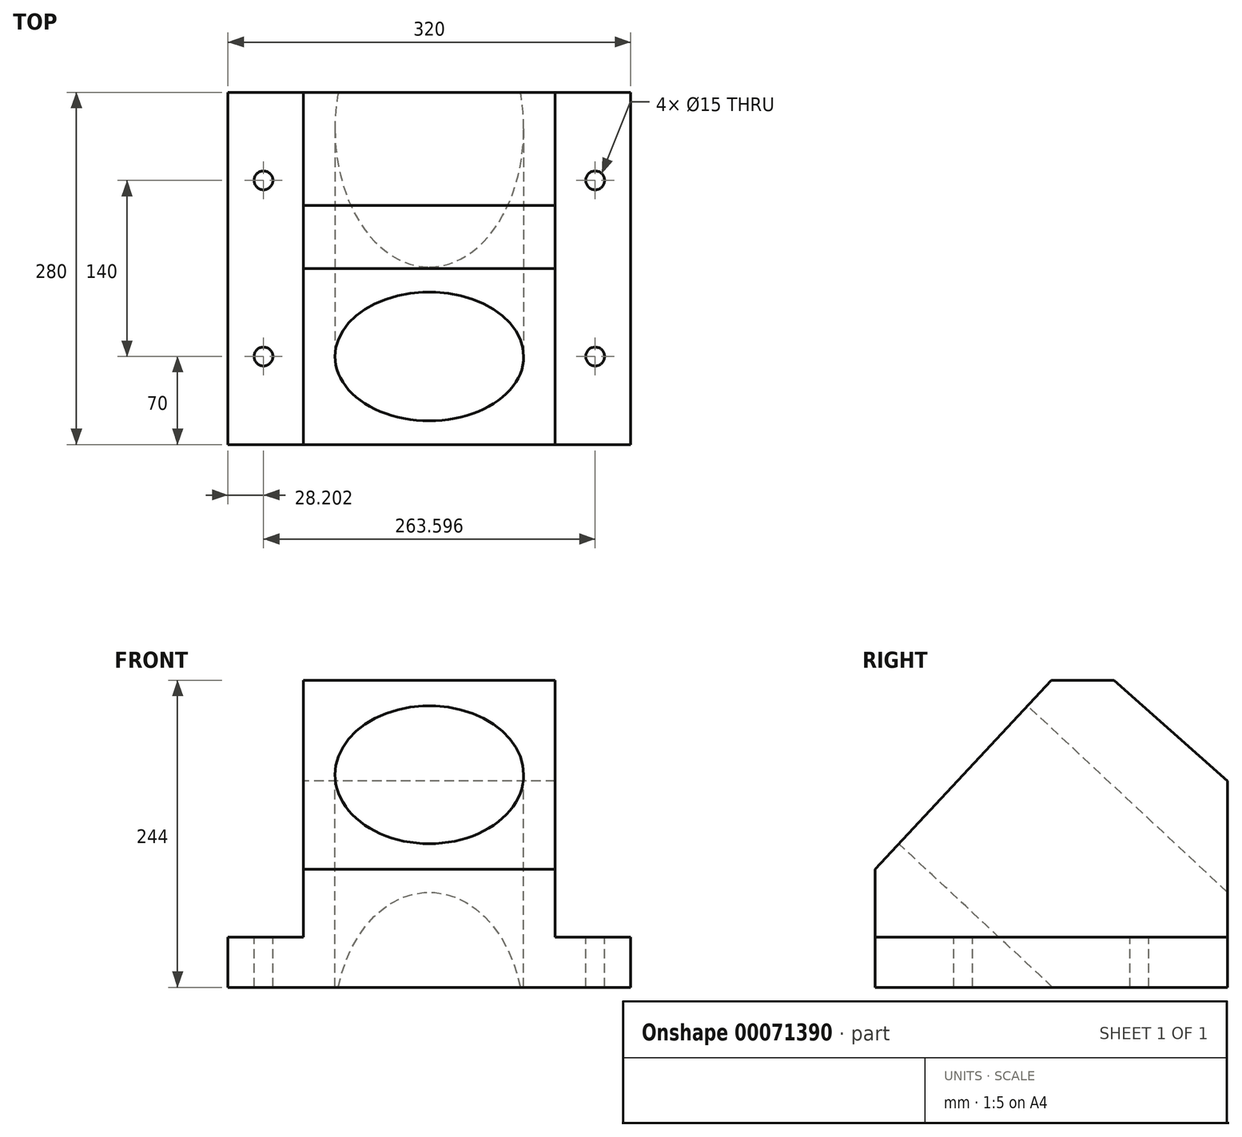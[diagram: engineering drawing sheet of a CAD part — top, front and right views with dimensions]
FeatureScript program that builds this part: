
annotation { "Feature Type Name" : "Feature", "Feature Type Description" : "" }
export const myFeature = defineFeature(function(context is Context, id is Id, definition is map)
    precondition{}
    {
        {
            var Q0;
            Q0=qCreatedBy(makeId("Right.planeOp"),FACE);
            var sketch = newSketch(context, id + "F0", { "sketchPlane" : qUnion([Q0])});
            skLineSegment(sketch, "E0", {"start": v(-140, -32.48) * mm, "end": v(140, -32.48) * mm});
            skLineSegment(sketch, "E1", {"start": v(-140, -32.48) * mm, "end": v(-140, 7.52) * mm});
            skLineSegment(sketch, "E2", {"start": v(-140, 7.52) * mm, "end": v(140, 7.52) * mm});
            skLineSegment(sketch, "E3", {"start": v(140, 7.52) * mm, "end": v(140, -32.48) * mm});
            skLineSegment(sketch, "E4", {"start": v(-140, 7.52) * mm, "end": v(-140, 61.52) * mm});
            skLineSegment(sketch, "E5", {"start": v(140, 7.52) * mm, "end": v(140, 131.52) * mm});
            skLineSegment(sketch, "E6", {"start": v(0, 211.52) * mm, "end": v(50, 211.52) * mm});
            skLineSegment(sketch, "E7", {"start": v(50, 211.52) * mm, "end": v(140, 131.52) * mm});
            skLineSegment(sketch, "E8", {"start": v(0, 211.52) * mm, "end": v(-140, 61.52) * mm});
            skSolve(sketch);
        }
        {
            var Q0;
            Q0=makeQuery(id+"F0.imprint","IMPRINT",FACE,{"disambiguationData":[TD([[makeQuery(id+"F0.imprint","IMPRINT",EDGE,{"derivedFrom":sQuery(id+"F0.wireOp",EDGE,"E0")}),1.0]])]});
            extrude(context, id + "F1", {"entities" : qUnion([Q0]), "depth" : 320 * mm, "symmetric" : true});
        }
        {
            var Q0;
            Q0=makeQuery(id+"F0.imprint","IMPRINT",FACE,{"disambiguationData":[TD([[makeQuery(id+"F0.imprint","IMPRINT",EDGE,{"derivedFrom":sQuery(id+"F0.wireOp",EDGE,"E2")}),1.0]])]});
            extrude(context, id + "F2", {"entities" : qUnion([Q0]), "operationType" : NewBodyOperationType.ADD, "depth" : 200 * mm, "symmetric" : true});
        }
        {
            var Q0;
            {var subQ2=sQuery(id+"F0.wireOp",EDGE,"E2");var subQ3=sQuery(id+"F0.wireOp",EDGE,"E1");var subQ4=sQuery(id+"F0.wireOp",EDGE,"E3");Q0=makeQuery(id+"F2.boolean.opBoolean","SPLIT",FACE,{"disambiguationData":[TD([makeQuery(id+"F1.opExtrude","CAP_FACE",FACE,{"disambiguationData":[OSD([sQuery(id+"F0.wireOp",EDGE,"E0"),subQ3,subQ2,subQ4])],"isStart":true})])],"derivedFrom":makeQuery(id+"F1.opExtrude","SWEPT_FACE",FACE,{"disambiguationData":[OSD([subQ2])]})});}
            var sketch = newSketch(context, id + "F3", { "sketchPlane" : qUnion([Q0])});
            skCircle(sketch, "E9", {"center": v(-131.8, 70) * mm, "radius": 7.5 * mm});
            skCircle(sketch, "E10", {"center": v(-131.8, -70) * mm, "radius": 7.5 * mm});
            skCircle(sketch, "E11.MirrorC", {"center": v(131.8, 70) * mm, "radius": 7.5 * mm});
            skCircle(sketch, "E12.MirrorC", {"center": v(131.8, -70) * mm, "radius": 7.5 * mm});
            skSolve(sketch);
        }
        {
            var Q0;
            Q0 = qSketchRegion(id + "F3", true);
            extrude(context, id + "F4", {"entities" : qUnion([Q0]), "operationType" : NewBodyOperationType.REMOVE, "oppositeDirection" : true, "depth" : 50 * mm});
        }
        {
            var Q0;
            Q0=makeQuery(id+"F2.opExtrude","SWEPT_FACE",FACE,{"disambiguationData":[OSD([sQuery(id+"F0.wireOp",EDGE,"E8")])]});
            var sketch = newSketch(context, id + "F5", { "sketchPlane" : qUnion([Q0])});
            skCircle(sketch, "E13", {"center": v(0, 52.04) * mm, "radius": 75 * mm});
            skSolve(sketch);
        }
        {
            var Q0;
            Q0 = qSketchRegion(id + "F5", true);
            extrude(context, id + "F6", {"entities" : qUnion([Q0]), "operationType" : NewBodyOperationType.REMOVE, "oppositeDirection" : true, "depth" : 421.5 * mm});
        }
    });
